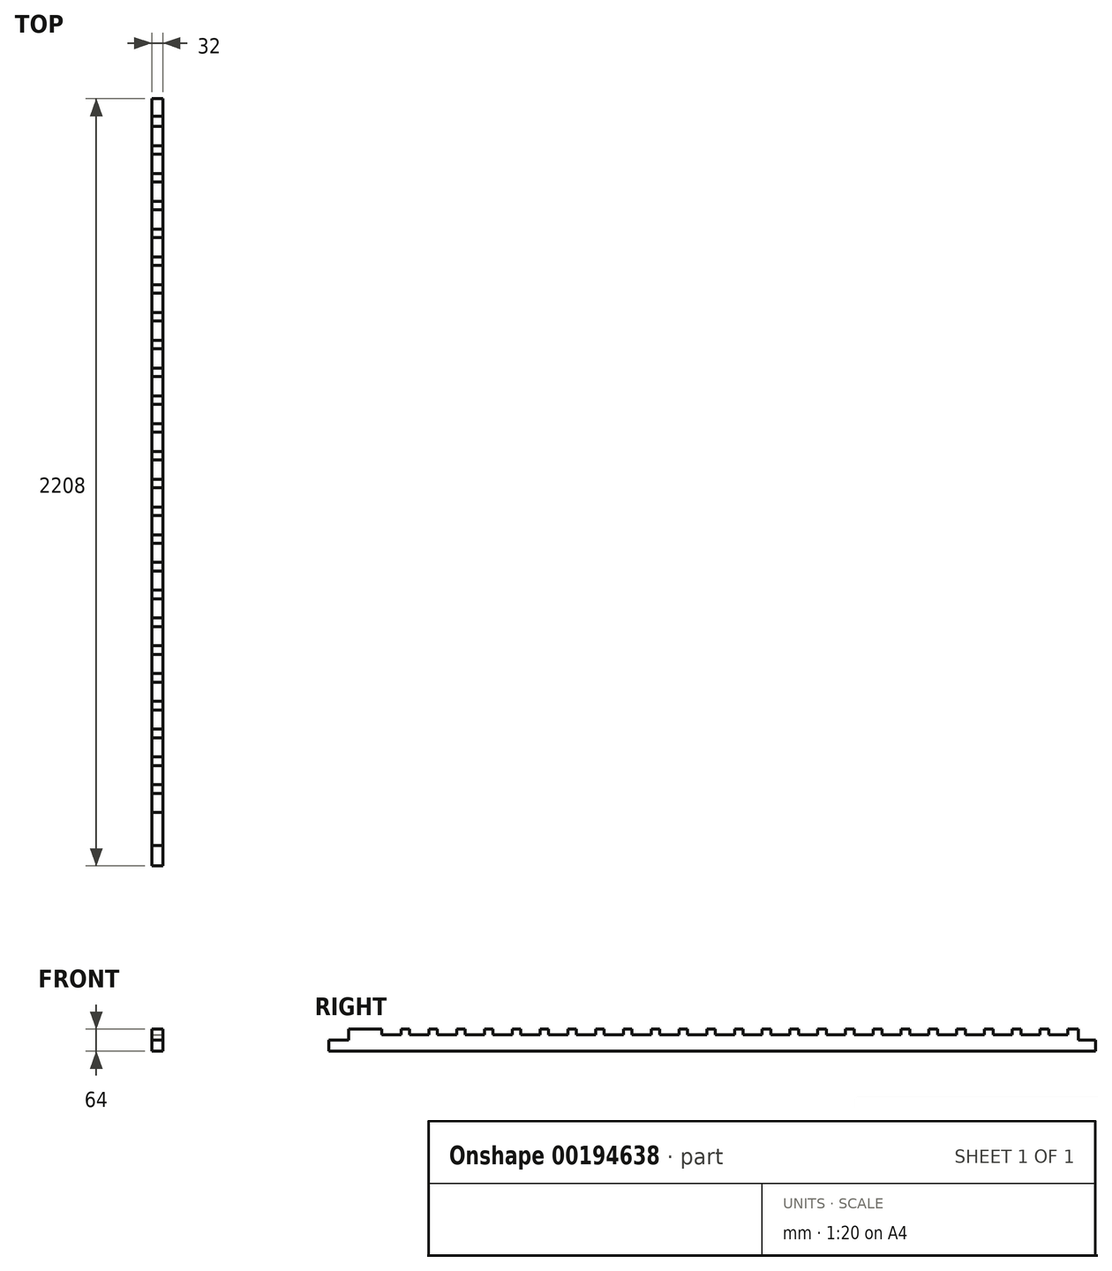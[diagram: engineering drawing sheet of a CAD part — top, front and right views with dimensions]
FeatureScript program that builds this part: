
annotation { "Feature Type Name" : "Feature", "Feature Type Description" : "" }
export const myFeature = defineFeature(function(context is Context, id is Id, definition is map)
    precondition{}
    {
        {
            var Q0;
            Q0=qCreatedBy(makeId("Front.planeOp"),FACE);
            var sketch = newSketch(context, id + "F0", { "sketchPlane" : qUnion([Q0])});
            skLineSegment(sketch, "E0.bottom", {"start": v(-16, 16) * mm, "end": v(16, 16) * mm});
            skLineSegment(sketch, "E0.top", {"start": v(-16, -16) * mm, "end": v(16, -16) * mm});
            skLineSegment(sketch, "E0.left", {"start": v(-16, 16) * mm, "end": v(-16, -16) * mm});
            skLineSegment(sketch, "E0.right", {"start": v(16, 16) * mm, "end": v(16, -16) * mm});
            skPoint(sketch, "E0.middle", {"position": v(0, 0) * mm});
            skSolve(sketch);
        }
        {
            var Q0;
            Q0=makeQuery(id+"F0.imprint","IMPRINT",FACE,{"disambiguationData":[TD([[makeQuery(id+"F0.imprint","IMPRINT",EDGE,{"derivedFrom":sQuery(id+"F0.wireOp",EDGE,"E0.bottom")}),-1.0]])]});
            extrude(context, id + "F1", {"entities" : qUnion([Q0]), "depth" : (2300 - 12 - 80) * mm});
        }
        {
            var Q0;
            Q0=qCreatedBy(makeId("Front.planeOp"),FACE);
            cPlane(context, id + "F2", {"entities" : qUnion([Q0]), "cplaneType" : CPlaneType.OFFSET, "offset" : 50 * mm, "width" : 150 * mm, "height" : 150 * mm});
        }
        {
            var Q0;
            Q0=qCreatedBy(id+"F2.planeOp",FACE);
            var sketch = newSketch(context, id + "F3", { "sketchPlane" : qUnion([Q0])});
            skLineSegment(sketch, "E1.bottom", {"start": v(16, 48) * mm, "end": v(-16, 48) * mm});
            skLineSegment(sketch, "E1.top", {"start": v(16, 16) * mm, "end": v(-16, 16) * mm});
            skLineSegment(sketch, "E1.left", {"start": v(16, 48) * mm, "end": v(16, 16) * mm});
            skLineSegment(sketch, "E1.right", {"start": v(-16, 48) * mm, "end": v(-16, 16) * mm});
            skPoint(sketch, "E1.middle", {"position": v(0, 32) * mm});
            skSolve(sketch);
        }
        {
            var Q0;
            Q0=makeQuery(id+"F3.imprint","IMPRINT",FACE,{"disambiguationData":[TD([[makeQuery(id+"F3.imprint","IMPRINT",EDGE,{"derivedFrom":sQuery(id+"F3.wireOp",EDGE,"E1.bottom")}),1.0]])]});
            extrude(context, id + "F4", {"entities" : qUnion([Q0]), "operationType" : NewBodyOperationType.ADD, "depth" : 2100 * mm});
        }
        {
            var Q0;
            Q0=makeQuery(id+"F4.opExtrude","SWEPT_FACE",FACE,{"disambiguationData":[OSD([sQuery(id+"F3.wireOp",EDGE,"E1.left")])]});
            var sketch = newSketch(context, id + "F5", { "sketchPlane" : qUnion([Q0])});
            skLineSegment(sketch, "E2.0", {"start": v(-135, 32) * mm, "end": v(-80, 32) * mm});
            skLineSegment(sketch, "E3.0", {"start": v(-80, 52) * mm, "end": v(-80, 32) * mm});
            skLineSegment(sketch, "E4.0", {"start": v(-135, 52) * mm, "end": v(-135, 32) * mm});
            skLineSegment(sketch, "E5", {"start": v(-135, 52) * mm, "end": v(-80, 52) * mm});
            skLineSegment(sketch, "E6.1.0.0", {"start": v(-215, 52) * mm, "end": v(-160, 52) * mm});
            skLineSegment(sketch, "E6.1.0.1", {"start": v(-160, 52) * mm, "end": v(-160, 32) * mm});
            skLineSegment(sketch, "E6.1.0.2", {"start": v(-215, 32) * mm, "end": v(-160, 32) * mm});
            skLineSegment(sketch, "E6.1.0.3", {"start": v(-215, 52) * mm, "end": v(-215, 32) * mm});
            skLineSegment(sketch, "E6.2.0.0", {"start": v(-295, 52) * mm, "end": v(-240, 52) * mm});
            skLineSegment(sketch, "E6.2.0.1", {"start": v(-240, 52) * mm, "end": v(-240, 32) * mm});
            skLineSegment(sketch, "E6.2.0.2", {"start": v(-295, 32) * mm, "end": v(-240, 32) * mm});
            skLineSegment(sketch, "E6.2.0.3", {"start": v(-295, 52) * mm, "end": v(-295, 32) * mm});
            skLineSegment(sketch, "E6.direction1", {"start": v(-135, 52) * mm, "end": v(-215, 52) * mm, "construction": true});
            skLineSegment(sketch, "E7.0.3.0", {"start": v(-375, 52) * mm, "end": v(-320, 52) * mm});
            skLineSegment(sketch, "E7.3.3.0", {"start": v(-320, 52) * mm, "end": v(-320, 32) * mm});
            skLineSegment(sketch, "E7.6.3.0", {"start": v(-375, 32) * mm, "end": v(-320, 32) * mm});
            skLineSegment(sketch, "E7.9.3.0", {"start": v(-375, 52) * mm, "end": v(-375, 32) * mm});
            skLineSegment(sketch, "E7.0.4.0", {"start": v(-455, 52) * mm, "end": v(-400, 52) * mm});
            skLineSegment(sketch, "E7.3.4.0", {"start": v(-400, 52) * mm, "end": v(-400, 32) * mm});
            skLineSegment(sketch, "E7.6.4.0", {"start": v(-455, 32) * mm, "end": v(-400, 32) * mm});
            skLineSegment(sketch, "E7.9.4.0", {"start": v(-455, 52) * mm, "end": v(-455, 32) * mm});
            skLineSegment(sketch, "E7.0.5.0", {"start": v(-535, 52) * mm, "end": v(-480, 52) * mm});
            skLineSegment(sketch, "E7.3.5.0", {"start": v(-480, 52) * mm, "end": v(-480, 32) * mm});
            skLineSegment(sketch, "E7.6.5.0", {"start": v(-535, 32) * mm, "end": v(-480, 32) * mm});
            skLineSegment(sketch, "E7.9.5.0", {"start": v(-535, 52) * mm, "end": v(-535, 32) * mm});
            skLineSegment(sketch, "E7.0.6.0", {"start": v(-615, 52) * mm, "end": v(-560, 52) * mm});
            skLineSegment(sketch, "E7.3.6.0", {"start": v(-560, 52) * mm, "end": v(-560, 32) * mm});
            skLineSegment(sketch, "E7.6.6.0", {"start": v(-615, 32) * mm, "end": v(-560, 32) * mm});
            skLineSegment(sketch, "E7.9.6.0", {"start": v(-615, 52) * mm, "end": v(-615, 32) * mm});
            skLineSegment(sketch, "E7.0.7.0", {"start": v(-695, 52) * mm, "end": v(-640, 52) * mm});
            skLineSegment(sketch, "E7.3.7.0", {"start": v(-640, 52) * mm, "end": v(-640, 32) * mm});
            skLineSegment(sketch, "E7.6.7.0", {"start": v(-695, 32) * mm, "end": v(-640, 32) * mm});
            skLineSegment(sketch, "E7.9.7.0", {"start": v(-695, 52) * mm, "end": v(-695, 32) * mm});
            skLineSegment(sketch, "E7.0.8.0", {"start": v(-775, 52) * mm, "end": v(-720, 52) * mm});
            skLineSegment(sketch, "E7.3.8.0", {"start": v(-720, 52) * mm, "end": v(-720, 32) * mm});
            skLineSegment(sketch, "E7.6.8.0", {"start": v(-775, 32) * mm, "end": v(-720, 32) * mm});
            skLineSegment(sketch, "E7.9.8.0", {"start": v(-775, 52) * mm, "end": v(-775, 32) * mm});
            skLineSegment(sketch, "E7.0.9.0", {"start": v(-855, 52) * mm, "end": v(-800, 52) * mm});
            skLineSegment(sketch, "E7.3.9.0", {"start": v(-800, 52) * mm, "end": v(-800, 32) * mm});
            skLineSegment(sketch, "E7.6.9.0", {"start": v(-855, 32) * mm, "end": v(-800, 32) * mm});
            skLineSegment(sketch, "E7.9.9.0", {"start": v(-855, 52) * mm, "end": v(-855, 32) * mm});
            skLineSegment(sketch, "E7.0.10.0", {"start": v(-935, 52) * mm, "end": v(-880, 52) * mm});
            skLineSegment(sketch, "E7.3.10.0", {"start": v(-880, 52) * mm, "end": v(-880, 32) * mm});
            skLineSegment(sketch, "E7.6.10.0", {"start": v(-935, 32) * mm, "end": v(-880, 32) * mm});
            skLineSegment(sketch, "E7.9.10.0", {"start": v(-935, 52) * mm, "end": v(-935, 32) * mm});
            skLineSegment(sketch, "E7.0.11.0", {"start": v(-1015, 52) * mm, "end": v(-960, 52) * mm});
            skLineSegment(sketch, "E7.3.11.0", {"start": v(-960, 52) * mm, "end": v(-960, 32) * mm});
            skLineSegment(sketch, "E7.6.11.0", {"start": v(-1015, 32) * mm, "end": v(-960, 32) * mm});
            skLineSegment(sketch, "E7.9.11.0", {"start": v(-1015, 52) * mm, "end": v(-1015, 32) * mm});
            skLineSegment(sketch, "E7.0.12.0", {"start": v(-1095, 52) * mm, "end": v(-1040, 52) * mm});
            skLineSegment(sketch, "E7.3.12.0", {"start": v(-1040, 52) * mm, "end": v(-1040, 32) * mm});
            skLineSegment(sketch, "E7.6.12.0", {"start": v(-1095, 32) * mm, "end": v(-1040, 32) * mm});
            skLineSegment(sketch, "E7.9.12.0", {"start": v(-1095, 52) * mm, "end": v(-1095, 32) * mm});
            skLineSegment(sketch, "E7.0.13.0", {"start": v(-1175, 52) * mm, "end": v(-1120, 52) * mm});
            skLineSegment(sketch, "E7.3.13.0", {"start": v(-1120, 52) * mm, "end": v(-1120, 32) * mm});
            skLineSegment(sketch, "E7.6.13.0", {"start": v(-1175, 32) * mm, "end": v(-1120, 32) * mm});
            skLineSegment(sketch, "E7.9.13.0", {"start": v(-1175, 52) * mm, "end": v(-1175, 32) * mm});
            skLineSegment(sketch, "E7.0.14.0", {"start": v(-1255, 52) * mm, "end": v(-1200, 52) * mm});
            skLineSegment(sketch, "E7.3.14.0", {"start": v(-1200, 52) * mm, "end": v(-1200, 32) * mm});
            skLineSegment(sketch, "E7.6.14.0", {"start": v(-1255, 32) * mm, "end": v(-1200, 32) * mm});
            skLineSegment(sketch, "E7.9.14.0", {"start": v(-1255, 52) * mm, "end": v(-1255, 32) * mm});
            skLineSegment(sketch, "E8.0.15.0", {"start": v(-1335, 52) * mm, "end": v(-1280, 52) * mm});
            skLineSegment(sketch, "E8.3.15.0", {"start": v(-1280, 52) * mm, "end": v(-1280, 32) * mm});
            skLineSegment(sketch, "E8.6.15.0", {"start": v(-1335, 32) * mm, "end": v(-1280, 32) * mm});
            skLineSegment(sketch, "E8.9.15.0", {"start": v(-1335, 52) * mm, "end": v(-1335, 32) * mm});
            skLineSegment(sketch, "E8.0.16.0", {"start": v(-1415, 52) * mm, "end": v(-1360, 52) * mm});
            skLineSegment(sketch, "E8.3.16.0", {"start": v(-1360, 52) * mm, "end": v(-1360, 32) * mm});
            skLineSegment(sketch, "E8.6.16.0", {"start": v(-1415, 32) * mm, "end": v(-1360, 32) * mm});
            skLineSegment(sketch, "E8.9.16.0", {"start": v(-1415, 52) * mm, "end": v(-1415, 32) * mm});
            skLineSegment(sketch, "E8.0.17.0", {"start": v(-1495, 52) * mm, "end": v(-1440, 52) * mm});
            skLineSegment(sketch, "E8.3.17.0", {"start": v(-1440, 52) * mm, "end": v(-1440, 32) * mm});
            skLineSegment(sketch, "E8.6.17.0", {"start": v(-1495, 32) * mm, "end": v(-1440, 32) * mm});
            skLineSegment(sketch, "E8.9.17.0", {"start": v(-1495, 52) * mm, "end": v(-1495, 32) * mm});
            skLineSegment(sketch, "E8.0.18.0", {"start": v(-1575, 52) * mm, "end": v(-1520, 52) * mm});
            skLineSegment(sketch, "E8.3.18.0", {"start": v(-1520, 52) * mm, "end": v(-1520, 32) * mm});
            skLineSegment(sketch, "E8.6.18.0", {"start": v(-1575, 32) * mm, "end": v(-1520, 32) * mm});
            skLineSegment(sketch, "E8.9.18.0", {"start": v(-1575, 52) * mm, "end": v(-1575, 32) * mm});
            skLineSegment(sketch, "E8.0.19.0", {"start": v(-1655, 52) * mm, "end": v(-1600, 52) * mm});
            skLineSegment(sketch, "E8.3.19.0", {"start": v(-1600, 52) * mm, "end": v(-1600, 32) * mm});
            skLineSegment(sketch, "E8.6.19.0", {"start": v(-1655, 32) * mm, "end": v(-1600, 32) * mm});
            skLineSegment(sketch, "E8.9.19.0", {"start": v(-1655, 52) * mm, "end": v(-1655, 32) * mm});
            skLineSegment(sketch, "E8.0.20.0", {"start": v(-1735, 52) * mm, "end": v(-1680, 52) * mm});
            skLineSegment(sketch, "E8.3.20.0", {"start": v(-1680, 52) * mm, "end": v(-1680, 32) * mm});
            skLineSegment(sketch, "E8.6.20.0", {"start": v(-1735, 32) * mm, "end": v(-1680, 32) * mm});
            skLineSegment(sketch, "E8.9.20.0", {"start": v(-1735, 52) * mm, "end": v(-1735, 32) * mm});
            skLineSegment(sketch, "E8.0.21.0", {"start": v(-1815, 52) * mm, "end": v(-1760, 52) * mm});
            skLineSegment(sketch, "E8.3.21.0", {"start": v(-1760, 52) * mm, "end": v(-1760, 32) * mm});
            skLineSegment(sketch, "E8.6.21.0", {"start": v(-1815, 32) * mm, "end": v(-1760, 32) * mm});
            skLineSegment(sketch, "E8.9.21.0", {"start": v(-1815, 52) * mm, "end": v(-1815, 32) * mm});
            skLineSegment(sketch, "E8.0.22.0", {"start": v(-1895, 52) * mm, "end": v(-1840, 52) * mm});
            skLineSegment(sketch, "E8.3.22.0", {"start": v(-1840, 52) * mm, "end": v(-1840, 32) * mm});
            skLineSegment(sketch, "E8.6.22.0", {"start": v(-1895, 32) * mm, "end": v(-1840, 32) * mm});
            skLineSegment(sketch, "E8.9.22.0", {"start": v(-1895, 52) * mm, "end": v(-1895, 32) * mm});
            skLineSegment(sketch, "E8.0.23.0", {"start": v(-1975, 52) * mm, "end": v(-1920, 52) * mm});
            skLineSegment(sketch, "E8.3.23.0", {"start": v(-1920, 52) * mm, "end": v(-1920, 32) * mm});
            skLineSegment(sketch, "E8.6.23.0", {"start": v(-1975, 32) * mm, "end": v(-1920, 32) * mm});
            skLineSegment(sketch, "E8.9.23.0", {"start": v(-1975, 52) * mm, "end": v(-1975, 32) * mm});
            skLineSegment(sketch, "E8.0.24.0", {"start": v(-2055, 52) * mm, "end": v(-2000, 52) * mm});
            skLineSegment(sketch, "E8.3.24.0", {"start": v(-2000, 52) * mm, "end": v(-2000, 32) * mm});
            skLineSegment(sketch, "E8.6.24.0", {"start": v(-2055, 32) * mm, "end": v(-2000, 32) * mm});
            skLineSegment(sketch, "E8.9.24.0", {"start": v(-2055, 52) * mm, "end": v(-2055, 32) * mm});
            skSolve(sketch);
        }
        {
            var Q0;
            Q0 = qSketchRegion(id + "F5", true);
            extrude(context, id + "F6", {"entities" : qUnion([Q0]), "operationType" : NewBodyOperationType.REMOVE, "oppositeDirection" : true, "depth" : 32 * mm});
        }
    });
